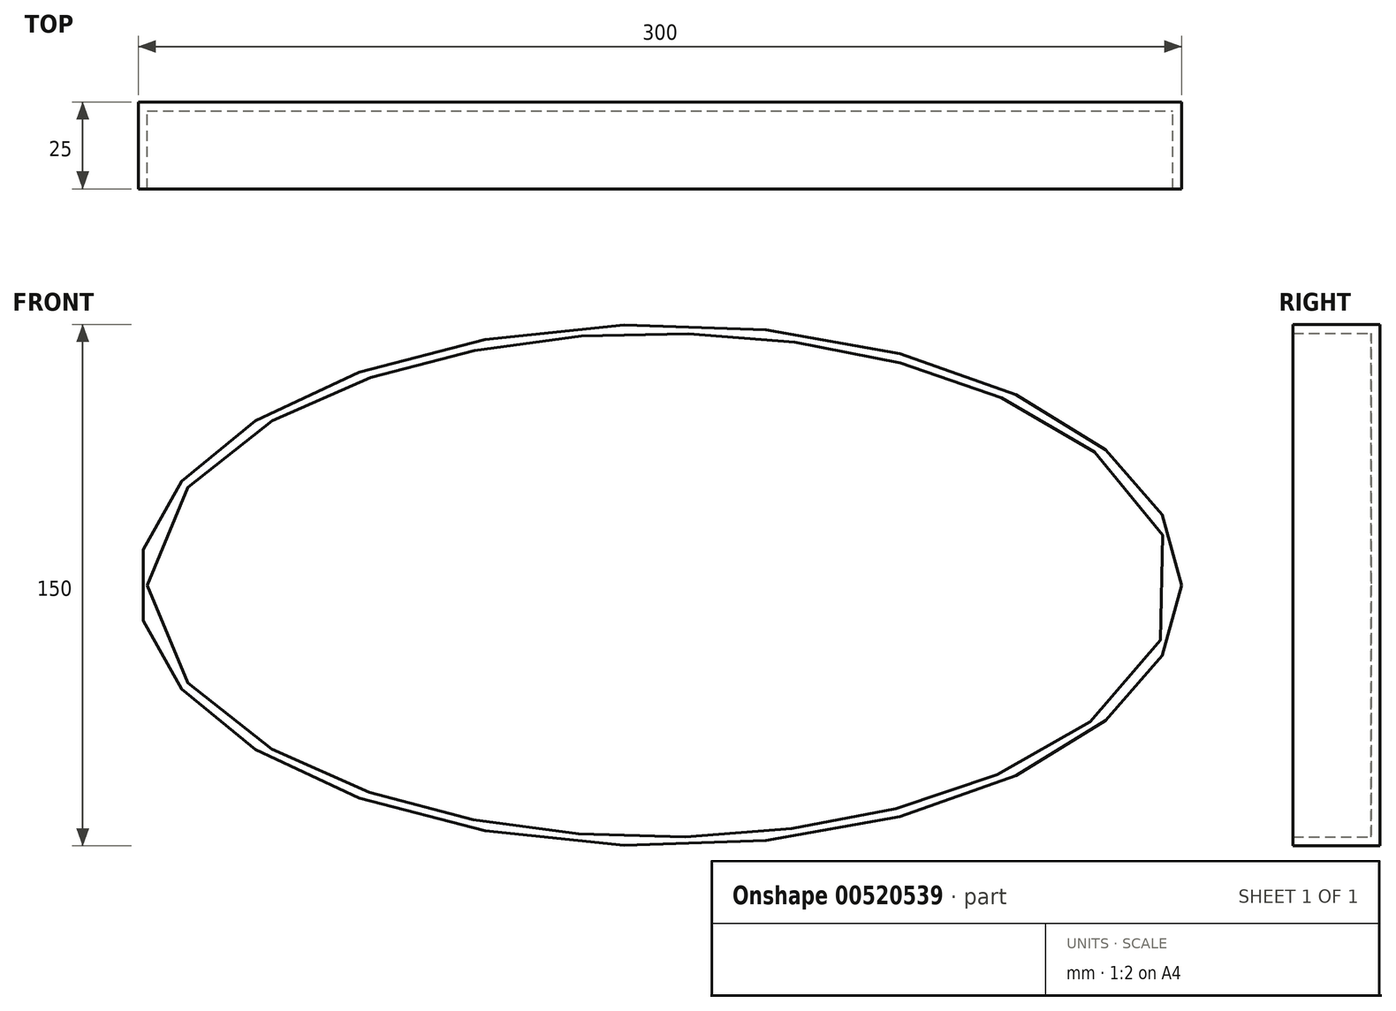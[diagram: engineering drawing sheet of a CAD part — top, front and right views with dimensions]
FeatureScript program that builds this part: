
annotation { "Feature Type Name" : "Feature", "Feature Type Description" : "" }
export const myFeature = defineFeature(function(context is Context, id is Id, definition is map)
    precondition{}
    {
        {
            var Q0;
            Q0=qCreatedBy(makeId("Front.planeOp"),FACE);
            var sketch = newSketch(context, id + "F0", { "sketchPlane" : qUnion([Q0])});
            skEllipse(sketch, "E0", {"center": v(0, 0) * mm, "majorRadius": 150 * mm, "minorRadius": 75 * mm, "majorAxis": v(1, 0)});
            skSolve(sketch);
        }
        {
            var Q0;
            Q0=makeQuery(id+"F0.imprint","IMPRINT",FACE,{"disambiguationData":[TD([[makeQuery(id+"F0.imprint","IMPRINT",EDGE,{"derivedFrom":sQuery(id+"F0.wireOp",EDGE,"E0")}),1.0]])]});
            extrude(context, id + "F1", {"entities" : qUnion([Q0]), "depth" : 25 * mm, "offsetDistance" : 25 * mm});
        }
        {
            var Q0;
            Q0=makeQuery(id+"F1.opExtrude","CAP_FACE",FACE,{"disambiguationData":[OSD([sQuery(id+"F0.wireOp",EDGE,"E0")])],"isStart":false});
            shell(context, id + "F2", {"entities" : qUnion([Q0]), "thickness" : 2.5 * mm});
        }
    });
